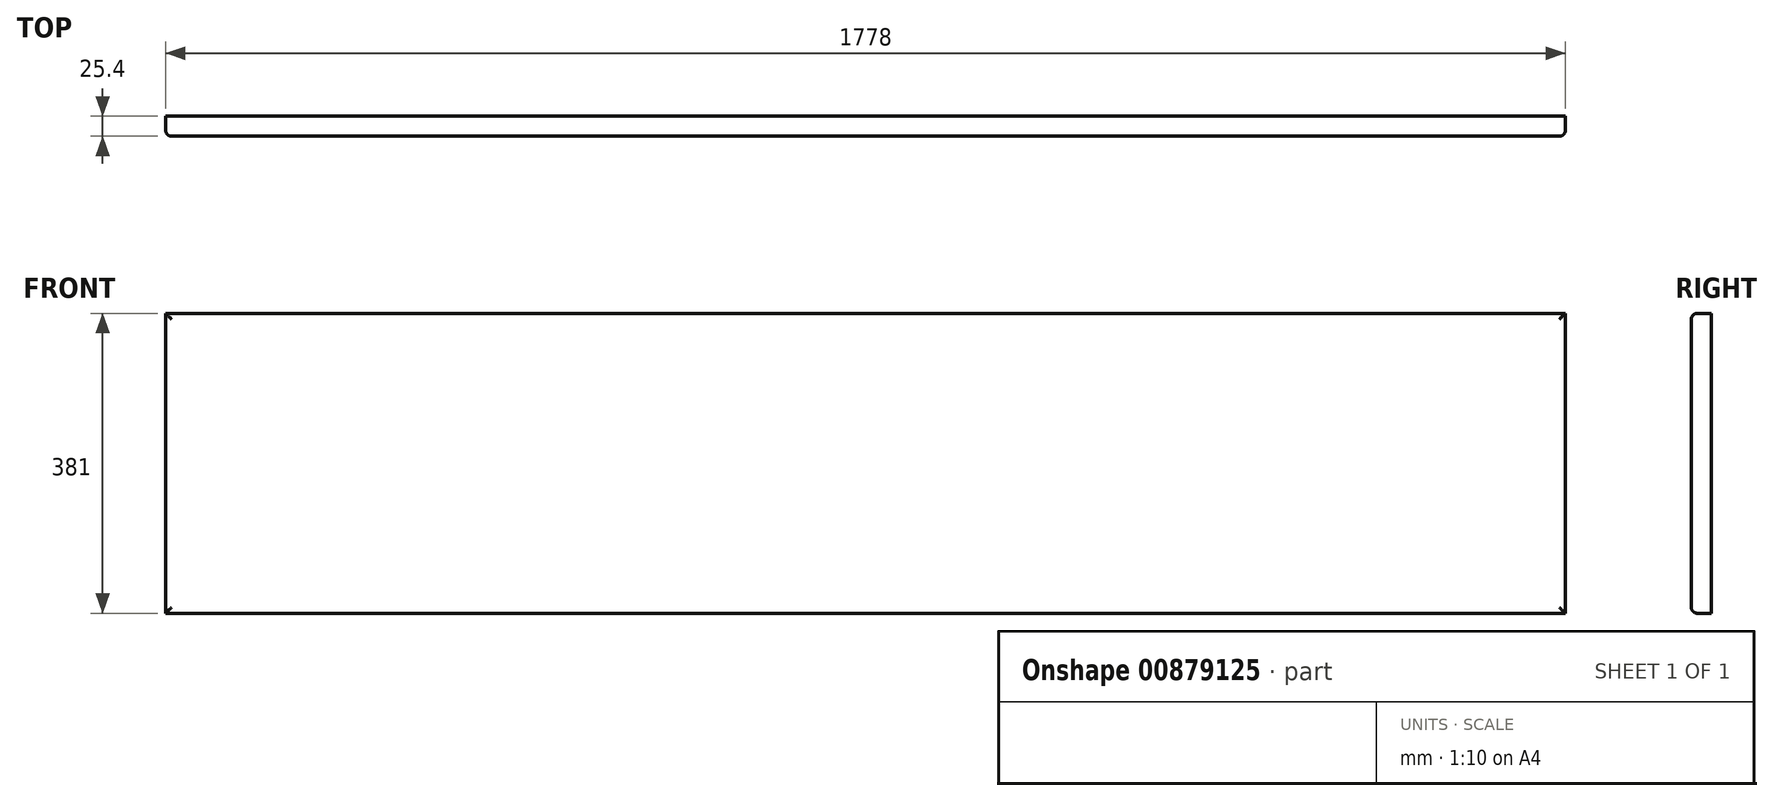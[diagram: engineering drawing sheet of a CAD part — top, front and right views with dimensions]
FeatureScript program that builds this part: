
annotation { "Feature Type Name" : "Feature", "Feature Type Description" : "" }
export const myFeature = defineFeature(function(context is Context, id is Id, definition is map)
    precondition{}
    {
        {
            var Q0;
            Q0=qCreatedBy(makeId("Front.planeOp"),FACE);
            var sketch = newSketch(context, id + "F0", { "sketchPlane" : qUnion([Q0])});
            skLineSegment(sketch, "E0.bottom", {"start": v(-889, 190.5) * mm, "end": v(889, 190.5) * mm});
            skLineSegment(sketch, "E0.top", {"start": v(-889, -190.5) * mm, "end": v(889, -190.5) * mm});
            skLineSegment(sketch, "E0.left", {"start": v(-889, 190.5) * mm, "end": v(-889, -190.5) * mm});
            skLineSegment(sketch, "E0.right", {"start": v(889, 190.5) * mm, "end": v(889, -190.5) * mm});
            skPoint(sketch, "E0.middle", {"position": v(0, 0) * mm});
            skSolve(sketch);
        }
        {
            var Q0;
            Q0=makeQuery(id+"F0.imprint","IMPRINT",FACE,{"disambiguationData":[TD([[makeQuery(id+"F0.imprint","IMPRINT",EDGE,{"derivedFrom":sQuery(id+"F0.wireOp",EDGE,"E0.bottom")}),-1.0]])]});
            extrude(context, id + "F1", {"entities" : qUnion([Q0]), "depth" : 25.4 * mm, "offsetDistance" : 25.4 * mm});
        }
        {
            var Q0;
            Q0=makeQuery(id+"F1.opExtrude","CAP_EDGE",EDGE,{"disambiguationData":[OSD([sQuery(id+"F0.wireOp",EDGE,"E0.left")])],"isStart":false});
            var Q1;
            Q1=makeQuery(id+"F1.opExtrude","CAP_EDGE",EDGE,{"disambiguationData":[OSD([sQuery(id+"F0.wireOp",EDGE,"E0.bottom")])],"isStart":false});
            var Q2;
            Q2=makeQuery(id+"F1.opExtrude","CAP_FACE",FACE,{"disambiguationData":[OSD([sQuery(id+"F0.wireOp",EDGE,"E0.bottom"),sQuery(id+"F0.wireOp",EDGE,"E0.top"),sQuery(id+"F0.wireOp",EDGE,"E0.left"),sQuery(id+"F0.wireOp",EDGE,"E0.right")])],"isStart":false});
            fillet(context, id + "F2", {"entities" : qUnion([Q0, Q1, Q2]), "radius" : 7.62 * mm, "tangentPropagation" : true, "allowEdgeOverflow" : false});
        }
    });
